# Revit family: РОСМА_МанометрКотловой
name_source: partatom
category: Арматура трубопроводов
revit_build: Autodesk Revit 2018 (Build: 20180423_1000(x64)
units: mm (PartAtom-declared; Revit-internal decimal feet)

## family parameters
Всегда вертикально = Да
На основе рабочей плоскости = Нет
Общий = Нет
При загрузке вырезать с полостями = Нет
Размер круглого соединителя = Использовать диаметр
Тип детали = Вставляется

## types (1)
- 810
    ADSK_Единица измерения = шт.
    ADSK_Количество = 1
    DN = 15.00 мм
    Ddempfer = 6 мм
    Dgol = 18 мм
    Drezba = М20
    Table = спец_котловой
    Table_2 = размеры_Котловой
    URL = https://rosma.spb.ru
    Группа модели = Оборудование
    Давление05 = ‎ : ТМ 0…0,25МПа
    Давление06 = ‎ : ТМ 0…0,4МПа
    Давление07 = ‎ : ТМ 0…0,6МПа
    Давление08 = ‎ : ТМ 0…1,0МПа
    Давление09 = ‎ : ТМ 0…1,6МПа
    Давление10 = ‎ : ТМ 0…2,5МПа
    Давление11 = ‎ : ТМ 0…4МПа
    Давление12 = ‎ : ТМ 0…6МПа
    Изготовитель = ЗАО "РОСМА"
    Исполнение = 810
    Класс точности = 1.5
    Климатическое исполнение = Группа В3 по ГОСТ Р 52931; климатическое исполнение УХЛ категории 3.1 по ГОСТ 15150
    Код IP = IP40
    Описание = Манометр показывающий ТМ серия 10, котловые.
    Присоединение = Радиальное
    Температура окружающей среды = от -60°С до +60°С
    Температура рабочей среды = от -50°С до +150°С
    Техническая документация = ТУ 4212-001-4719015564-2008; ГОСТ 2405–88
